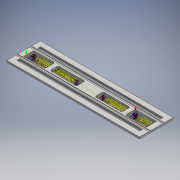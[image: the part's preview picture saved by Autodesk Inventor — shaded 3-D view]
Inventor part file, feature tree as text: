
AUTODESK INVENTOR PART (.ipt)
format: ipt  version: 2016 (Build 200138000, 138)  size: 1,546,752 bytes
history: native  units: mm
features: sketch x2, extrude x1, emboss x1
ambient origin geometry x8: Origin, YZ Plane, XZ Plane, XY Plane, X Axis, Y Axis, Z Axis, Center Point
bodies: Body1 (feature_tree)
feature tree (4):
  extrude  "Extrusion5"  Depth=8.0mm
  emboss  "Emboss6"
  sketch  "Sketch1"  dims[d0=135.4582mm d1=43.104285mm d4=21.585333mm d5=92.185791mm d8=8.0mm]
  sketch  "Sketch6"  dims[d9=8.0mm d10=8.0mm d48=3.175mm d49=3.175mm d50=50.779945mm d62=88.879945mm d63=19.05mm d64=50.779945mm d78=15.0mm d79=15.0mm d80=25.4mm d81=25.4mm d82=25.4mm d83=25.4mm d84=9.525mm d85=0.0mm d90=9.525mm d91=9.525mm d94=3.0mm d95=0.0mm]
